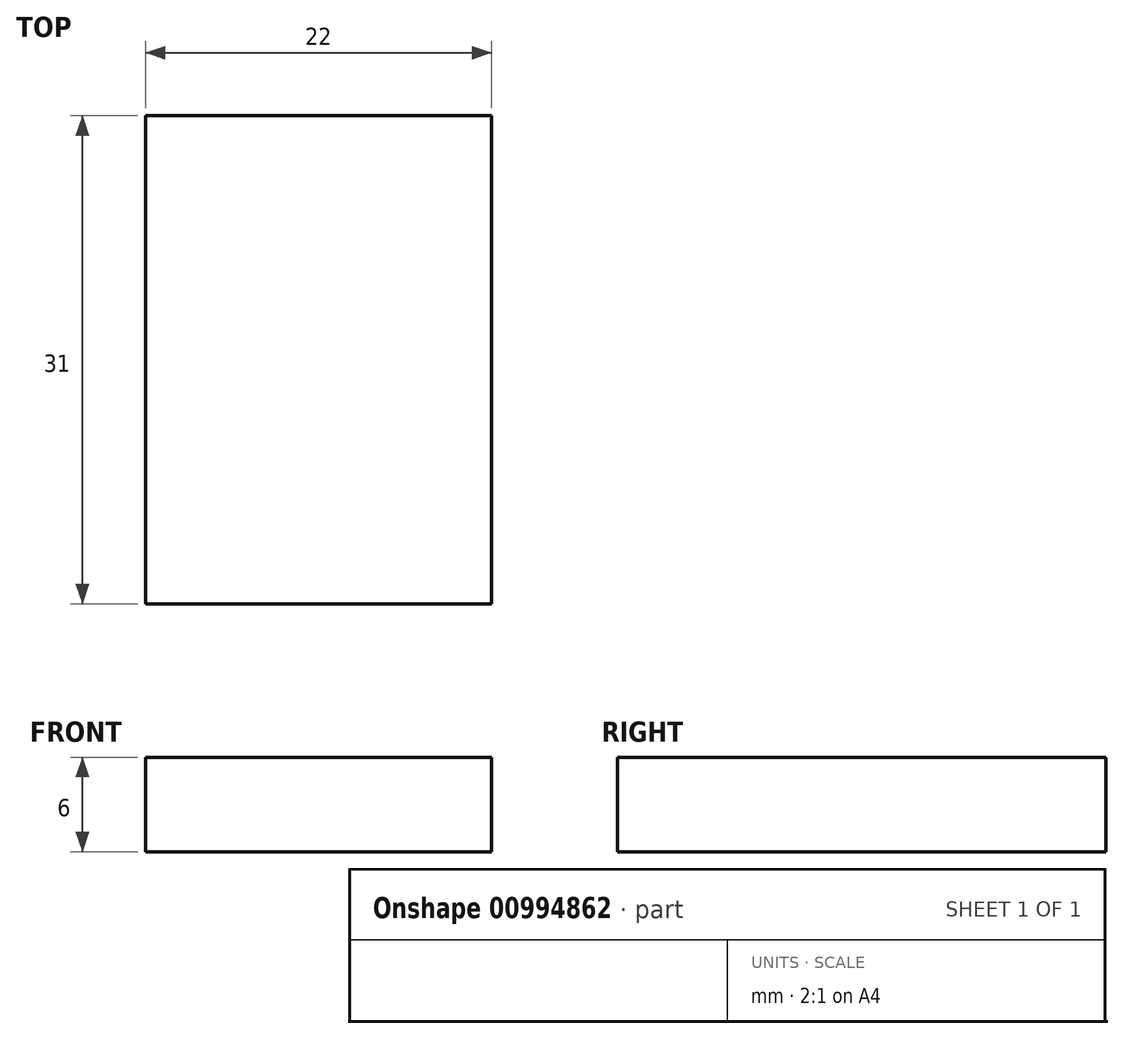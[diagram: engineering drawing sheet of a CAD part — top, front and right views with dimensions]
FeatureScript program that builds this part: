
annotation { "Feature Type Name" : "Feature", "Feature Type Description" : "" }
export const myFeature = defineFeature(function(context is Context, id is Id, definition is map)
    precondition{}
    {
        {
            var Q0;
            Q0=qCreatedBy(makeId("Top.planeOp"),FACE);
            var sketch = newSketch(context, id + "F0", { "sketchPlane" : qUnion([Q0])});
            skLineSegment(sketch, "E0.bottom", {"start": v(11, 15.5) * mm, "end": v(-11, 15.5) * mm});
            skLineSegment(sketch, "E0.top", {"start": v(11, -15.5) * mm, "end": v(-11, -15.5) * mm});
            skLineSegment(sketch, "E0.left", {"start": v(11, 15.5) * mm, "end": v(11, -15.5) * mm});
            skLineSegment(sketch, "E0.right", {"start": v(-11, 15.5) * mm, "end": v(-11, -15.5) * mm});
            skPoint(sketch, "E0.middle", {"position": v(0, 0) * mm});
            skSolve(sketch);
        }
        {
            var Q0;
            Q0 = qSketchRegion(id + "F0", true);
            extrude(context, id + "F1", {"entities" : qUnion([Q0]), "depth" : 6 * mm, "offsetDistance" : 25 * mm});
        }
    });
